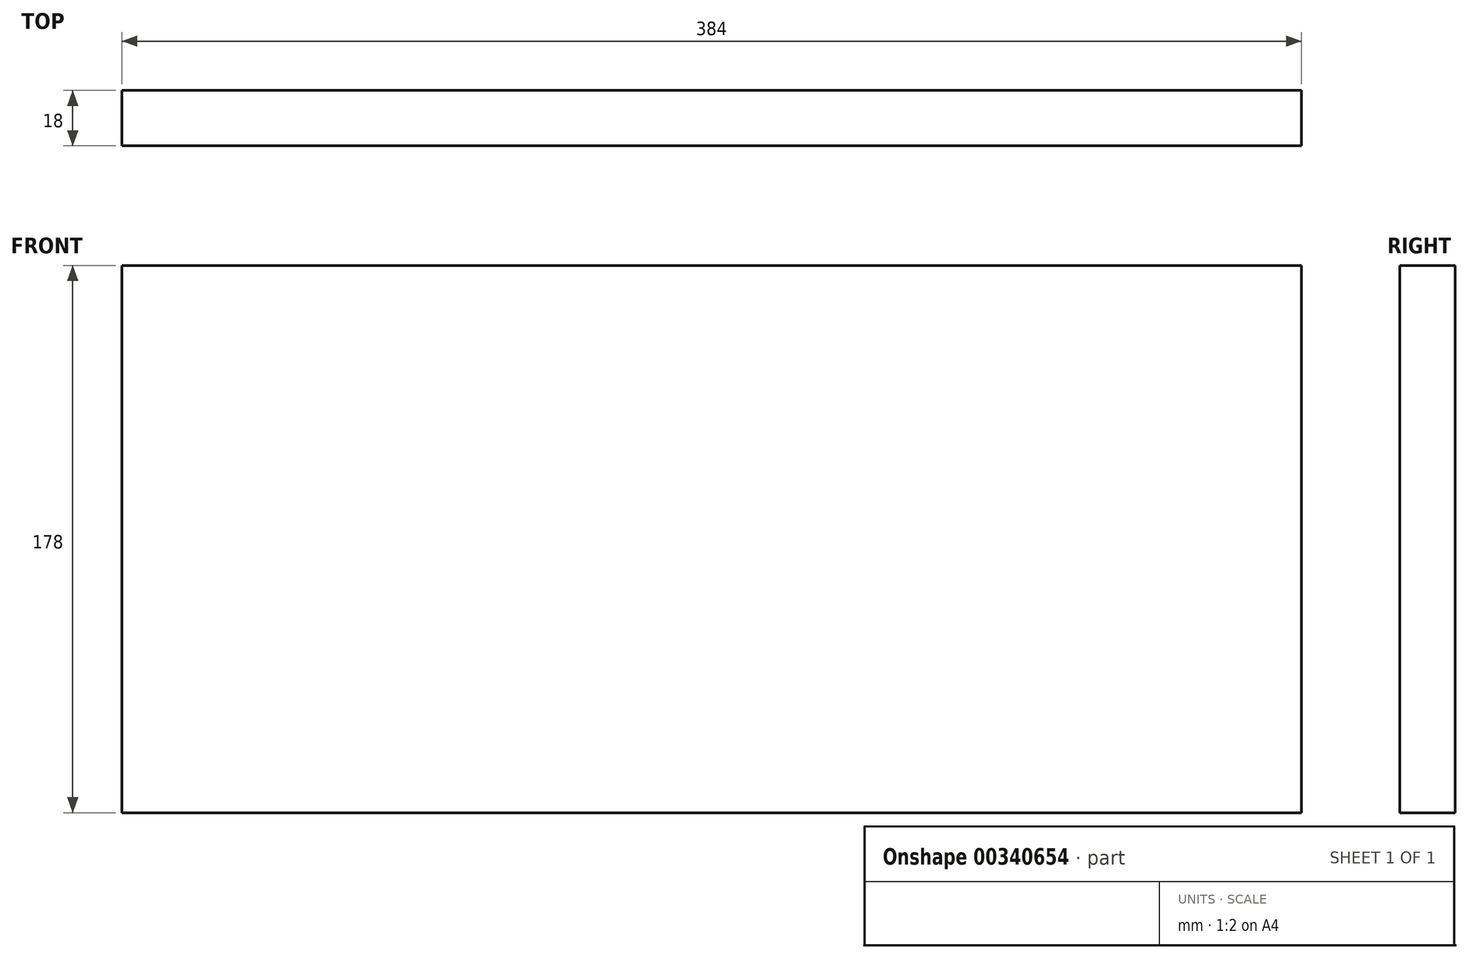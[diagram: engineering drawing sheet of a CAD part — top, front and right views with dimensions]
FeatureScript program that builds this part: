
annotation { "Feature Type Name" : "Feature", "Feature Type Description" : "" }
export const myFeature = defineFeature(function(context is Context, id is Id, definition is map)
    precondition{}
    {
        {
            var Q0;
            Q0=qCreatedBy(makeId("Front.planeOp"),FACE);
            var sketch = newSketch(context, id + "F0", { "sketchPlane" : qUnion([Q0])});
            skLineSegment(sketch, "E0.bottom", {"start": v(-185.17, 84.18) * mm, "end": v(198.83, 84.18) * mm});
            skLineSegment(sketch, "E0.top", {"start": v(-185.17, -93.82) * mm, "end": v(198.83, -93.82) * mm});
            skLineSegment(sketch, "E0.left", {"start": v(-185.17, 84.18) * mm, "end": v(-185.17, -93.82) * mm});
            skLineSegment(sketch, "E0.right", {"start": v(198.83, 84.18) * mm, "end": v(198.83, -93.82) * mm});
            skSolve(sketch);
        }
        {
            var Q0;
            Q0=makeQuery(id+"F0.imprint","IMPRINT",FACE,{"disambiguationData":[TD([[makeQuery(id+"F0.imprint","IMPRINT",EDGE,{"derivedFrom":sQuery(id+"F0.wireOp",EDGE,"E0.bottom")}),-1.0]])]});
            extrude(context, id + "F1", {"entities" : qUnion([Q0]), "oppositeDirection" : true, "depth" : 18 * mm});
        }
    });
